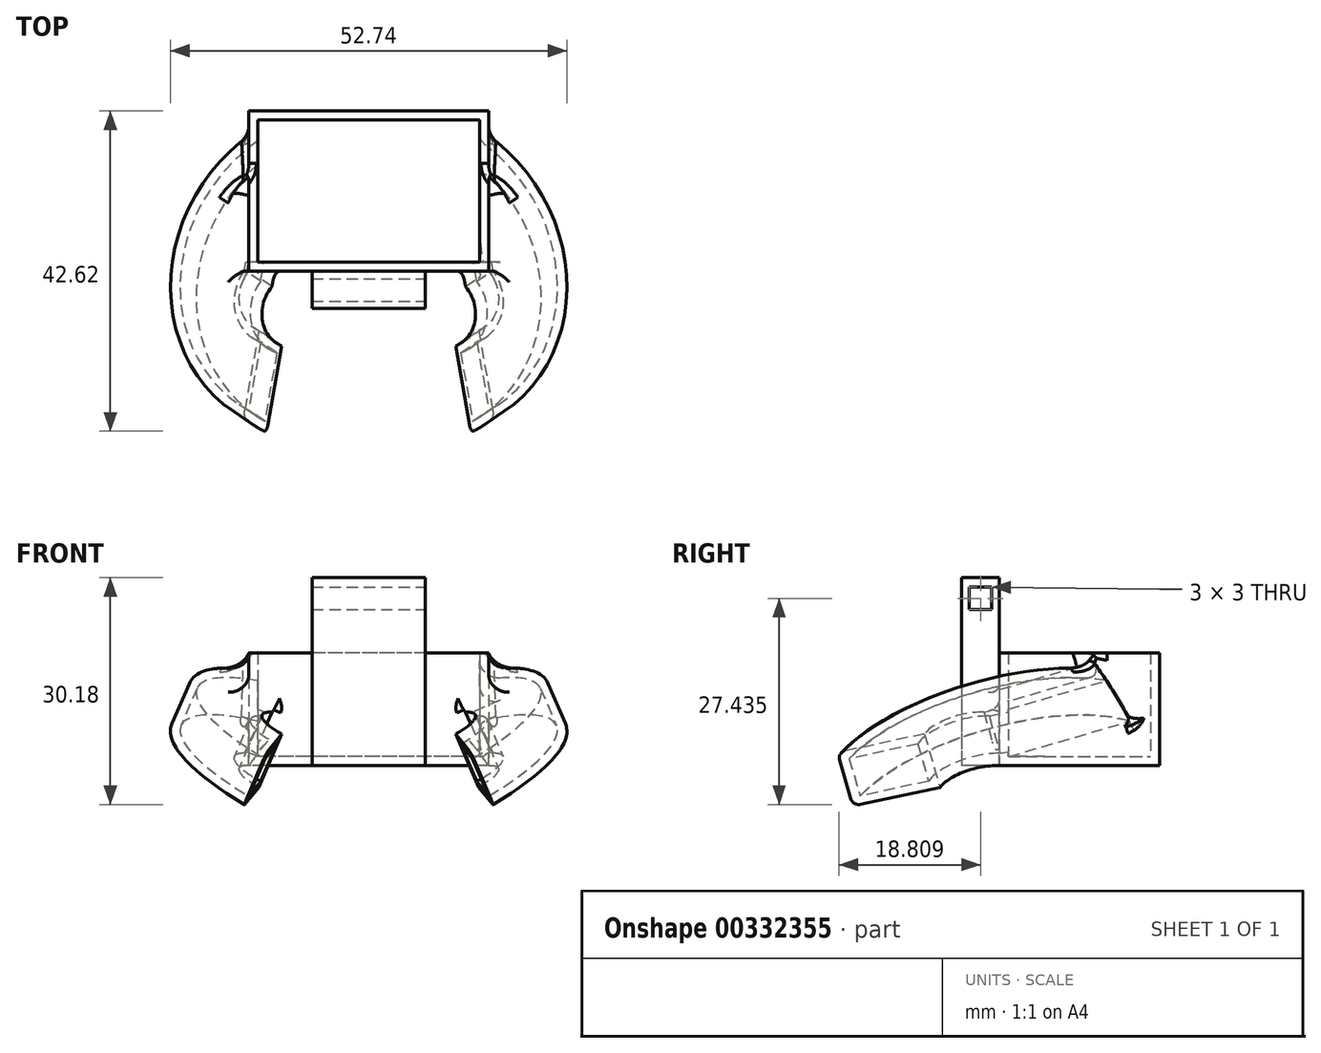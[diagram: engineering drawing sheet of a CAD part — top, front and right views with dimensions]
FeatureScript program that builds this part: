
annotation { "Feature Type Name" : "Feature", "Feature Type Description" : "" }
export const myFeature = defineFeature(function(context is Context, id is Id, definition is map)
    precondition{}
    {
        {
            var Q0;
            Q0=qCreatedBy(makeId("Top.planeOp"),FACE);
            var sketch = newSketch(context, id + "F0", { "sketchPlane" : qUnion([Q0])});
            skLineSegment(sketch, "E0.bottom", {"start": v(15.95, -10.65) * mm, "end": v(-15.95, -10.65) * mm});
            skLineSegment(sketch, "E0.top", {"start": v(15.95, 10.65) * mm, "end": v(-15.95, 10.65) * mm});
            skLineSegment(sketch, "E0.left", {"start": v(15.95, -10.65) * mm, "end": v(15.95, 10.65) * mm});
            skLineSegment(sketch, "E0.right", {"start": v(-15.95, -10.65) * mm, "end": v(-15.95, 10.65) * mm});
            skPoint(sketch, "E0.middle", {"position": v(0, 0) * mm});
            skLineSegment(sketch, "E1", {"start": v(-13, -24.65) * mm, "end": v(-13, -18.65) * mm});
            skLineSegment(sketch, "E2", {"start": v(-13, -24.65) * mm, "end": v(-13, -30.65) * mm});
            skLineSegment(sketch, "E3.MirrorCS", {"start": v(13, -24.65) * mm, "end": v(13, -18.65) * mm});
            skLineSegment(sketch, "E4.MirrorCS", {"start": v(13, -24.65) * mm, "end": v(13, -30.65) * mm});
            skArc(sketch, "E5", {"start": v(-15.95, -10.65) * mm, "mid": v(-16.46, -15.38) * mm, "end": v(-13, -18.65) * mm});
            skArc(sketch, "E6", {"start": v(-15.95, 10.65) * mm, "mid": v(-27.57, -10.94) * mm, "end": v(-13, -30.65) * mm});
            skArc(sketch, "E7.MirrorCS", {"start": v(15.95, 10.65) * mm, "mid": v(27.57, -10.94) * mm, "end": v(13, -30.65) * mm});
            skArc(sketch, "E8.MirrorCS", {"start": v(15.95, -10.65) * mm, "mid": v(16.46, -15.38) * mm, "end": v(13, -18.65) * mm});
            skSolve(sketch);
        }
        {
            var Q0;
            Q0=makeQuery(id+"F0.imprint","IMPRINT",FACE,{"disambiguationData":[TD([[makeQuery(id+"F0.imprint","IMPRINT",EDGE,{"derivedFrom":sQuery(id+"F0.wireOp",EDGE,"E0.bottom")}),-1.0]])]});
            extrude(context, id + "F1", {"entities" : qUnion([Q0]), "depth" : 15 * mm, "offsetDistance" : 25 * mm});
        }
        {
            var Q0;
            Q0=makeQuery(id+"F0.imprint","IMPRINT",FACE,{"disambiguationData":[TD([[makeQuery(id+"F0.imprint","IMPRINT",EDGE,{"derivedFrom":sQuery(id+"F0.wireOp",EDGE,"E0.right")}),1.0]])]});
            extrude(context, id + "F2", {"entities" : qUnion([Q0]), "depth" : 8 * mm, "offsetDistance" : 25 * mm});
        }
        {
            var Q0;
            Q0=makeQuery(id+"F2.opExtrude","SWEPT_BODY",BODY,{"disambiguationData":[OSD([sQuery(id+"F0.wireOp",EDGE,"E0.right"),sQuery(id+"F0.wireOp",EDGE,"E1"),sQuery(id+"F0.wireOp",EDGE,"E2"),sQuery(id+"F0.wireOp",EDGE,"GjkKXvnJ-jA0g-s26r-HWS4-I9semydN4EE0"),sQuery(id+"F0.wireOp",EDGE,"CBcXbAIJ-9305-cYkE-zvGn-Y6aC1Gbph8QT")])]});
            var Q1;
            Q1=sQuery(id+"F0.wireOp",EDGE,"E0.right");
            transform(context, id + "F3", {"entities" : qUnion([Q0]), "transformType" : TransformType.ROTATION, "transformAxis" : qUnion([Q1]), "angle" : 25 * degree, "makeCopy" : false});
        }
        {
            var Q0;
            Q0=makeQuery(id+"F2.opExtrude","SWEPT_BODY",BODY,{"disambiguationData":[OSD([sQuery(id+"F0.wireOp",EDGE,"E0.right"),sQuery(id+"F0.wireOp",EDGE,"E1"),sQuery(id+"F0.wireOp",EDGE,"E2"),sQuery(id+"F0.wireOp",EDGE,"QFbH83jj-XYne-KEbY-MEjT-L67cxlXek1Lr"),sQuery(id+"F0.wireOp",EDGE,"gXgNoo7v-niw8-iljs-8967-YQMKxby19gpY")])]});
            var Q1;
            Q1=sQuery(id+"F0.wireOp",EDGE,"E0.bottom");
            transform(context, id + "F4", {"entities" : qUnion([Q0]), "transformType" : TransformType.ROTATION, "transformAxis" : qUnion([Q1]), "angle" : -12 * degree, "makeCopy" : false});
        }
        {
            var Q0;
            Q0=makeQuery(id+"F2.opExtrude","SWEPT_BODY",BODY,{"disambiguationData":[OSD([sQuery(id+"F0.wireOp",EDGE,"E0.right"),sQuery(id+"F0.wireOp",EDGE,"E1"),sQuery(id+"F0.wireOp",EDGE,"E2"),sQuery(id+"F0.wireOp",EDGE,"E5"),sQuery(id+"F0.wireOp",EDGE,"E6")])]});
            var Q1;
            Q1=makeQuery(id+"F1.opExtrude","SWEPT_EDGE",EDGE,{"disambiguationData":[OSD([sQuery(id+"F0.wireOp",EDGE,"E0.bottom"),sQuery(id+"F0.wireOp",EDGE,"E0.right"),sQuery(id+"F0.wireOp",EDGE,"E5")])]});
            transform(context, id + "F5", {"entities" : qUnion([Q0]), "transformType" : TransformType.ROTATION, "transformAxis" : qUnion([Q1]), "angle" : 10 * degree, "makeCopy" : false});
        }
        {
            var Q0;
            Q0=makeQuery(id+"F2.opExtrude","SWEPT_BODY",BODY,{"disambiguationData":[OSD([sQuery(id+"F0.wireOp",EDGE,"E0.right"),sQuery(id+"F0.wireOp",EDGE,"E1"),sQuery(id+"F0.wireOp",EDGE,"E2"),sQuery(id+"F0.wireOp",EDGE,"GjkKXvnJ-jA0g-s26r-HWS4-I9semydN4EE0"),sQuery(id+"F0.wireOp",EDGE,"CBcXbAIJ-9305-cYkE-zvGn-Y6aC1Gbph8QT")])]});
            var Q1;
            Q1=qCreatedBy(makeId("Right.planeOp"),FACE);
            mirror(context, id + "F6", {"operationType" : NewBodyOperationType.ADD, "entities" : qUnion([Q0]), "mirrorPlane" : qUnion([Q1])});
        }
        {
            var Q0;
            Q0=makeQuery(id+"F1.opExtrude","CAP_FACE",FACE,{"disambiguationData":[OSD([sQuery(id+"F0.wireOp",EDGE,"E0.bottom"),sQuery(id+"F0.wireOp",EDGE,"E0.top"),sQuery(id+"F0.wireOp",EDGE,"E0.left"),sQuery(id+"F0.wireOp",EDGE,"E0.right")])],"isStart":false});
            var Q1;
            Q1=makeQuery(id+"F2.opExtrude","SWEPT_FACE",FACE,{"disambiguationData":[OSD([sQuery(id+"F0.wireOp",EDGE,"E1"),sQuery(id+"F0.wireOp",EDGE,"E2")])]});
            var Q2;
            Q2=makeQuery(id+"F6.opPattern","COPY",FACE,{"derivedFrom":makeQuery(id+"F2.opExtrude","SWEPT_FACE",FACE,{"disambiguationData":[OSD([sQuery(id+"F0.wireOp",EDGE,"E1"),sQuery(id+"F0.wireOp",EDGE,"E2")])]}),"instanceName":"1"});
            shell(context, id + "F7", {"entities" : qUnion([Q0, Q1, Q2]), "thickness" : 1.2 * mm});
        }
        {
            var Q0;
            {var subQ0=sQuery(id+"F0.wireOp",EDGE,"E0.right");Q0=makeQuery(id+"F7.opShell","OFFSET_EDGE",EDGE,{"disambiguationData":[OSD([subQ0]),TDD([makeQuery(id+"F6.opPattern","COPY",EDGE,{"derivedFrom":makeQuery(id+"F2.opExtrude","CAP_EDGE",EDGE,{"disambiguationData":[OSD([subQ0])],"isStart":true}),"instanceName":"1"})])]});}
            var Q1;
            {var subQ0=sQuery(id+"F0.wireOp",EDGE,"E0.right");Q1=makeQuery(id+"F7.opShell","OFFSET_EDGE",EDGE,{"disambiguationData":[OSD([subQ0]),TDD([makeQuery(id+"F2.opExtrude","CAP_EDGE",EDGE,{"disambiguationData":[OSD([subQ0])],"isStart":true})])]});}
            var Q2;
            {var subQ0=sQuery(id+"F0.wireOp",EDGE,"gXgNoo7v-niw8-iljs-8967-YQMKxby19gpY");var subQ1=sQuery(id+"F0.wireOp",EDGE,"QFbH83jj-XYne-KEbY-MEjT-L67cxlXek1Lr");var subQ2=sQuery(id+"F0.wireOp",EDGE,"E2");var subQ3=sQuery(id+"F0.wireOp",EDGE,"E1");var subQ4=sQuery(id+"F0.wireOp",EDGE,"E0.right");Q2=makeQuery(id+"F7.opShell","OFFSET_EDGE",EDGE,{"disambiguationData":[OSD([subQ4,subQ3,subQ2,subQ1,subQ0]),TDD([makeQuery(id+"F6.boolean.opBoolean","INTERSECT",EDGE,{"derivedFrom":[makeQuery(id+"F1.opExtrude","SWEPT_FACE",FACE,{"disambiguationData":[OSD([subQ4])]}),makeQuery(id+"F2.opExtrude","CAP_FACE",FACE,{"disambiguationData":[OSD([subQ4,subQ3,subQ2,subQ1,subQ0])],"isStart":false})]})])]});}
            var Q3;
            Q3=makeQuery(id+"F7.opShell","OFFSET_EDGE",EDGE,{"disambiguationData":[OSD([sQuery(id+"F0.wireOp",EDGE,"E0.left"),sQuery(id+"F0.wireOp",EDGE,"E0.right"),sQuery(id+"F0.wireOp",EDGE,"E1"),sQuery(id+"F0.wireOp",EDGE,"E2"),sQuery(id+"F0.wireOp",EDGE,"QFbH83jj-XYne-KEbY-MEjT-L67cxlXek1Lr"),sQuery(id+"F0.wireOp",EDGE,"gXgNoo7v-niw8-iljs-8967-YQMKxby19gpY")])]});
            fillet(context, id + "F8", {"entities" : qUnion([Q0, Q1, Q2, Q3]), "tangentPropagation" : true, "radius" : 2 * mm, "defaultsChanged" : true, "vertexSettings" : [], "allowEdgeOverflow" : false});
        }
        {
            var Q0;
            Q0=makeQuery(id+"F0.imprint","IMPRINT",FACE,{"disambiguationData":[TD([[makeQuery(id+"F0.imprint","IMPRINT",EDGE,{"derivedFrom":sQuery(id+"F0.wireOp",EDGE,"E0.bottom")}),-1.0]])]});
            var sketch = newSketch(context, id + "F9", { "sketchPlane" : qUnion([Q0])});
            skLineSegment(sketch, "E9.bottom", {"start": v(7.54, -10.65) * mm, "end": v(-7.54, -10.65) * mm});
            skLineSegment(sketch, "E9.top", {"start": v(7.54, -15.65) * mm, "end": v(-7.54, -15.65) * mm});
            skLineSegment(sketch, "E9.left", {"start": v(7.54, -10.65) * mm, "end": v(7.54, -15.65) * mm});
            skLineSegment(sketch, "E9.right", {"start": v(-7.54, -10.65) * mm, "end": v(-7.54, -15.65) * mm});
            skPoint(sketch, "E9.middle", {"position": v(0, -13.15) * mm});
            skSolve(sketch);
        }
        {
            var Q0;
            {var subQ0=sQuery(id+"F9.wireOp",EDGE,"E9.top");Q0=makeQuery(id+"F9.imprint","IMPRINT",FACE,{"disambiguationData":[TD([[makeQuery(id+"F9.imprint","IMPRINT",EDGE,{"derivedFrom":subQ0}),-1.0]])]});}
            extrude(context, id + "F10", {"entities" : qUnion([Q0]), "operationType" : NewBodyOperationType.ADD, "depth" : 25 * mm, "offsetDistance" : 25 * mm});
        }
        {
            var Q0;
            Q0=makeQuery(id+"F10.opExtrude","SWEPT_FACE",FACE,{"disambiguationData":[OSD([sQuery(id+"F9.wireOp",EDGE,"E9.left")])]});
            var sketch = newSketch(context, id + "F11", { "sketchPlane" : qUnion([Q0])});
            skLineSegment(sketch, "E10.bottom", {"start": v(-11.66, 20.76) * mm, "end": v(-14.66, 20.76) * mm});
            skLineSegment(sketch, "E10.top", {"start": v(-11.66, 23.76) * mm, "end": v(-14.66, 23.76) * mm});
            skLineSegment(sketch, "E10.left", {"start": v(-11.66, 20.76) * mm, "end": v(-11.66, 23.76) * mm});
            skLineSegment(sketch, "E10.right", {"start": v(-14.66, 20.76) * mm, "end": v(-14.66, 23.76) * mm});
            skPoint(sketch, "E10.middle", {"position": v(-13.16, 22.26) * mm});
            skSolve(sketch);
        }
        {
            var Q0;
            Q0=makeQuery(id+"F11.imprint","IMPRINT",FACE,{"disambiguationData":[TD([[makeQuery(id+"F11.imprint","IMPRINT",EDGE,{"derivedFrom":sQuery(id+"F11.wireOp",EDGE,"E10.bottom")}),-1.0]])]});
            extrude(context, id + "F12", {"entities" : qUnion([Q0]), "operationType" : NewBodyOperationType.REMOVE, "oppositeDirection" : true, "depth" : 25 * mm, "offsetDistance" : 25 * mm});
        }
        {
            var Q0;
            Q0=makeQuery(id+"F6.boolean.opBoolean","INTERSECT",EDGE,{"derivedFrom":[makeQuery(id+"F1.opExtrude","SWEPT_FACE",FACE,{"disambiguationData":[OSD([sQuery(id+"F0.wireOp",EDGE,"E0.left")])]}),makeQuery(id+"F6.opPattern","COPY",FACE,{"derivedFrom":makeQuery(id+"F2.opExtrude","CAP_FACE",FACE,{"disambiguationData":[OSD([sQuery(id+"F0.wireOp",EDGE,"E0.right"),sQuery(id+"F0.wireOp",EDGE,"E1"),sQuery(id+"F0.wireOp",EDGE,"E2"),sQuery(id+"F0.wireOp",EDGE,"E5"),sQuery(id+"F0.wireOp",EDGE,"E6")])],"isStart":false}),"instanceName":"1"})]});
            var Q1;
            Q1=makeQuery(id+"F6.boolean.opBoolean","INTERSECT",EDGE,{"derivedFrom":[makeQuery(id+"F1.opExtrude","SWEPT_FACE",FACE,{"disambiguationData":[OSD([sQuery(id+"F0.wireOp",EDGE,"E0.left")])]}),makeQuery(id+"F6.opPattern","COPY",FACE,{"derivedFrom":makeQuery(id+"F2.opExtrude","SWEPT_FACE",FACE,{"disambiguationData":[OSD([sQuery(id+"F0.wireOp",EDGE,"E6")])]}),"instanceName":"1"})]});
            var Q2;
            Q2=makeQuery(id+"F6.boolean.opBoolean","INTERSECT",EDGE,{"derivedFrom":[makeQuery(id+"F1.opExtrude","SWEPT_FACE",FACE,{"disambiguationData":[OSD([sQuery(id+"F0.wireOp",EDGE,"E0.bottom")])]}),makeQuery(id+"F6.opPattern","COPY",FACE,{"derivedFrom":makeQuery(id+"F2.opExtrude","CAP_FACE",FACE,{"disambiguationData":[OSD([sQuery(id+"F0.wireOp",EDGE,"E0.right"),sQuery(id+"F0.wireOp",EDGE,"E1"),sQuery(id+"F0.wireOp",EDGE,"E2"),sQuery(id+"F0.wireOp",EDGE,"E5"),sQuery(id+"F0.wireOp",EDGE,"E6")])],"isStart":false}),"instanceName":"1"})]});
            var Q3;
            Q3=makeQuery(id+"F6.boolean.opBoolean","INTERSECT",EDGE,{"derivedFrom":[makeQuery(id+"F1.opExtrude","SWEPT_FACE",FACE,{"disambiguationData":[OSD([sQuery(id+"F0.wireOp",EDGE,"E0.bottom")])]}),makeQuery(id+"F2.opExtrude","CAP_FACE",FACE,{"disambiguationData":[OSD([sQuery(id+"F0.wireOp",EDGE,"E0.right"),sQuery(id+"F0.wireOp",EDGE,"E1"),sQuery(id+"F0.wireOp",EDGE,"E2"),sQuery(id+"F0.wireOp",EDGE,"E5"),sQuery(id+"F0.wireOp",EDGE,"E6")])],"isStart":false})]});
            var Q4;
            {var subQ0=sQuery(id+"F0.wireOp",EDGE,"E0.right");Q4=makeQuery(id+"F6.boolean.opBoolean","INTERSECT",EDGE,{"derivedFrom":[makeQuery(id+"F1.opExtrude","SWEPT_FACE",FACE,{"disambiguationData":[OSD([subQ0])]}),makeQuery(id+"F2.opExtrude","CAP_FACE",FACE,{"disambiguationData":[OSD([subQ0,sQuery(id+"F0.wireOp",EDGE,"E1"),sQuery(id+"F0.wireOp",EDGE,"E2"),sQuery(id+"F0.wireOp",EDGE,"E5"),sQuery(id+"F0.wireOp",EDGE,"E6")])],"isStart":false})]});}
            var Q5;
            Q5=makeQuery(id+"F6.boolean.opBoolean","INTERSECT",EDGE,{"derivedFrom":[makeQuery(id+"F1.opExtrude","SWEPT_FACE",FACE,{"disambiguationData":[OSD([sQuery(id+"F0.wireOp",EDGE,"E0.right")])]}),makeQuery(id+"F2.opExtrude","SWEPT_FACE",FACE,{"disambiguationData":[OSD([sQuery(id+"F0.wireOp",EDGE,"E6")])]})]});
            fillet(context, id + "F13", {"entities" : qUnion([Q0, Q1, Q2, Q3, Q4, Q5]), "tangentPropagation" : true, "radius" : 2 * mm, "defaultsChanged" : false, "vertexSettings" : [], "allowEdgeOverflow" : false});
        }
        {
            var Q0;
            Q0=makeQuery(id+"F6.boolean.opBoolean","INTERSECT",EDGE,{"derivedFrom":[makeQuery(id+"F1.opExtrude","SWEPT_FACE",FACE,{"disambiguationData":[OSD([sQuery(id+"F0.wireOp",EDGE,"E0.left")])]}),makeQuery(id+"F6.opPattern","COPY",FACE,{"derivedFrom":makeQuery(id+"F2.opExtrude","CAP_FACE",FACE,{"disambiguationData":[OSD([sQuery(id+"F0.wireOp",EDGE,"E0.right"),sQuery(id+"F0.wireOp",EDGE,"E1"),sQuery(id+"F0.wireOp",EDGE,"E2"),sQuery(id+"F0.wireOp",EDGE,"E5"),sQuery(id+"F0.wireOp",EDGE,"E6")])],"isStart":true}),"instanceName":"1"})]});
            var Q1;
            Q1=makeQuery(id+"F6.boolean.opBoolean","INTERSECT",EDGE,{"derivedFrom":[makeQuery(id+"F1.opExtrude","SWEPT_FACE",FACE,{"disambiguationData":[OSD([sQuery(id+"F0.wireOp",EDGE,"E0.bottom")])]}),makeQuery(id+"F6.opPattern","COPY",FACE,{"derivedFrom":makeQuery(id+"F2.opExtrude","SWEPT_FACE",FACE,{"disambiguationData":[OSD([sQuery(id+"F0.wireOp",EDGE,"E0.right")])]}),"instanceName":"1"})]});
            var Q2;
            Q2=makeQuery(id+"F6.boolean.opBoolean","INTERSECT",EDGE,{"derivedFrom":[makeQuery(id+"F1.opExtrude","SWEPT_FACE",FACE,{"disambiguationData":[OSD([sQuery(id+"F0.wireOp",EDGE,"E0.bottom")])]}),makeQuery(id+"F2.opExtrude","SWEPT_FACE",FACE,{"disambiguationData":[OSD([sQuery(id+"F0.wireOp",EDGE,"E0.right")])]})]});
            var Q3;
            {var subQ0=sQuery(id+"F0.wireOp",EDGE,"E0.right");Q3=makeQuery(id+"F6.boolean.opBoolean","INTERSECT",EDGE,{"derivedFrom":[makeQuery(id+"F1.opExtrude","SWEPT_FACE",FACE,{"disambiguationData":[OSD([subQ0])]}),makeQuery(id+"F2.opExtrude","CAP_FACE",FACE,{"disambiguationData":[OSD([subQ0,sQuery(id+"F0.wireOp",EDGE,"E1"),sQuery(id+"F0.wireOp",EDGE,"E2"),sQuery(id+"F0.wireOp",EDGE,"E5"),sQuery(id+"F0.wireOp",EDGE,"E6")])],"isStart":true})]});}
            var Q4;
            Q4=makeQuery(id+"F6.opPattern","COPY",EDGE,{"derivedFrom":makeQuery(id+"F2.opExtrude","CAP_EDGE",EDGE,{"disambiguationData":[OSD([sQuery(id+"F0.wireOp",EDGE,"E6")])],"isStart":false}),"instanceName":"1"});
            var Q5;
            Q5=makeQuery(id+"F6.opPattern","COPY",EDGE,{"derivedFrom":makeQuery(id+"F2.opExtrude","CAP_EDGE",EDGE,{"disambiguationData":[OSD([sQuery(id+"F0.wireOp",EDGE,"E6")])],"isStart":true}),"instanceName":"1"});
            var Q6;
            Q6=makeQuery(id+"F2.opExtrude","CAP_EDGE",EDGE,{"disambiguationData":[OSD([sQuery(id+"F0.wireOp",EDGE,"E6")])],"isStart":false});
            var Q7;
            Q7=makeQuery(id+"F2.opExtrude","CAP_EDGE",EDGE,{"disambiguationData":[OSD([sQuery(id+"F0.wireOp",EDGE,"E6")])],"isStart":true});
            fillet(context, id + "F14", {"entities" : qUnion([Q0, Q1, Q2, Q3, Q4, Q5, Q6, Q7]), "tangentPropagation" : true, "radius" : 1 * mm, "defaultsChanged" : false, "vertexSettings" : [], "allowEdgeOverflow" : false});
        }
    });
